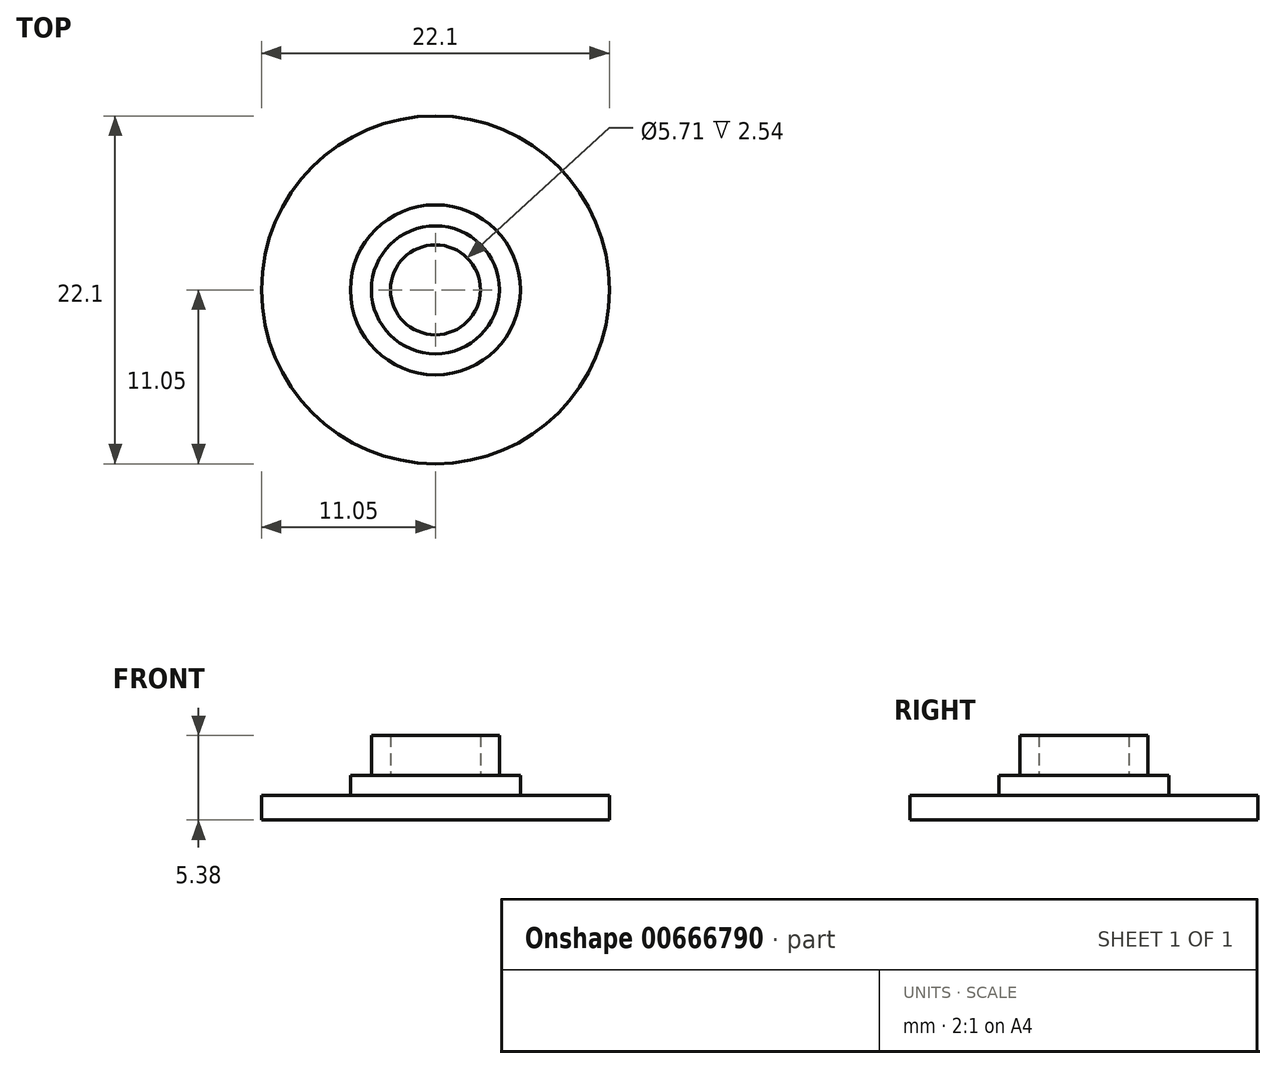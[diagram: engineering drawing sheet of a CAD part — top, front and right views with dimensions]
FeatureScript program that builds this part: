
annotation { "Feature Type Name" : "Feature", "Feature Type Description" : "" }
export const myFeature = defineFeature(function(context is Context, id is Id, definition is map)
    precondition{}
    {
        {
            var Q0;
            Q0=qCreatedBy(makeId("Top.planeOp"),FACE);
            var sketch = newSketch(context, id + "F0", { "sketchPlane" : qUnion([Q0])});
            skCircle(sketch, "E0", {"center": v(0, 0) * mm, "radius": 11.05 * mm});
            skSolve(sketch);
        }
        {
            var Q0;
            Q0 = qSketchRegion(id + "F0", true);
            extrude(context, id + "F1", {"entities" : qUnion([Q0]), "depth" : 1.57 * mm, "offsetDistance" : 25.4 * mm});
        }
        {
            var Q0;
            Q0=makeQuery(id+"F1.opExtrude","CAP_FACE",FACE,{"disambiguationData":[OSD([sQuery(id+"F0.wireOp",EDGE,"E0")])],"isStart":false});
            var sketch = newSketch(context, id + "F2", { "sketchPlane" : qUnion([Q0])});
            skCircle(sketch, "E1", {"center": v(0, 0) * mm, "radius": 5.4 * mm});
            skSolve(sketch);
        }
        {
            var Q0;
            Q0 = qSketchRegion(id + "F2", true);
            extrude(context, id + "F3", {"entities" : qUnion([Q0]), "operationType" : NewBodyOperationType.ADD, "depth" : 1.27 * mm, "offsetDistance" : 25.4 * mm});
        }
        {
            var Q0;
            Q0=makeQuery(id+"F3.opExtrude","CAP_FACE",FACE,{"disambiguationData":[OSD([sQuery(id+"F2.wireOp",EDGE,"E1")])],"isStart":false});
            var sketch = newSketch(context, id + "F4", { "sketchPlane" : qUnion([Q0])});
            skCircle(sketch, "E2", {"center": v(0, 0) * mm, "radius": 4.06 * mm});
            skCircle(sketch, "E3", {"center": v(0, 0) * mm, "radius": 2.86 * mm});
            skSolve(sketch);
        }
        {
            var Q0;
            Q0 = qSketchRegion(id + "F4", true);
            extrude(context, id + "F5", {"entities" : qUnion([Q0]), "operationType" : NewBodyOperationType.ADD, "depth" : 2.54 * mm, "offsetDistance" : 25.4 * mm});
        }
    });
